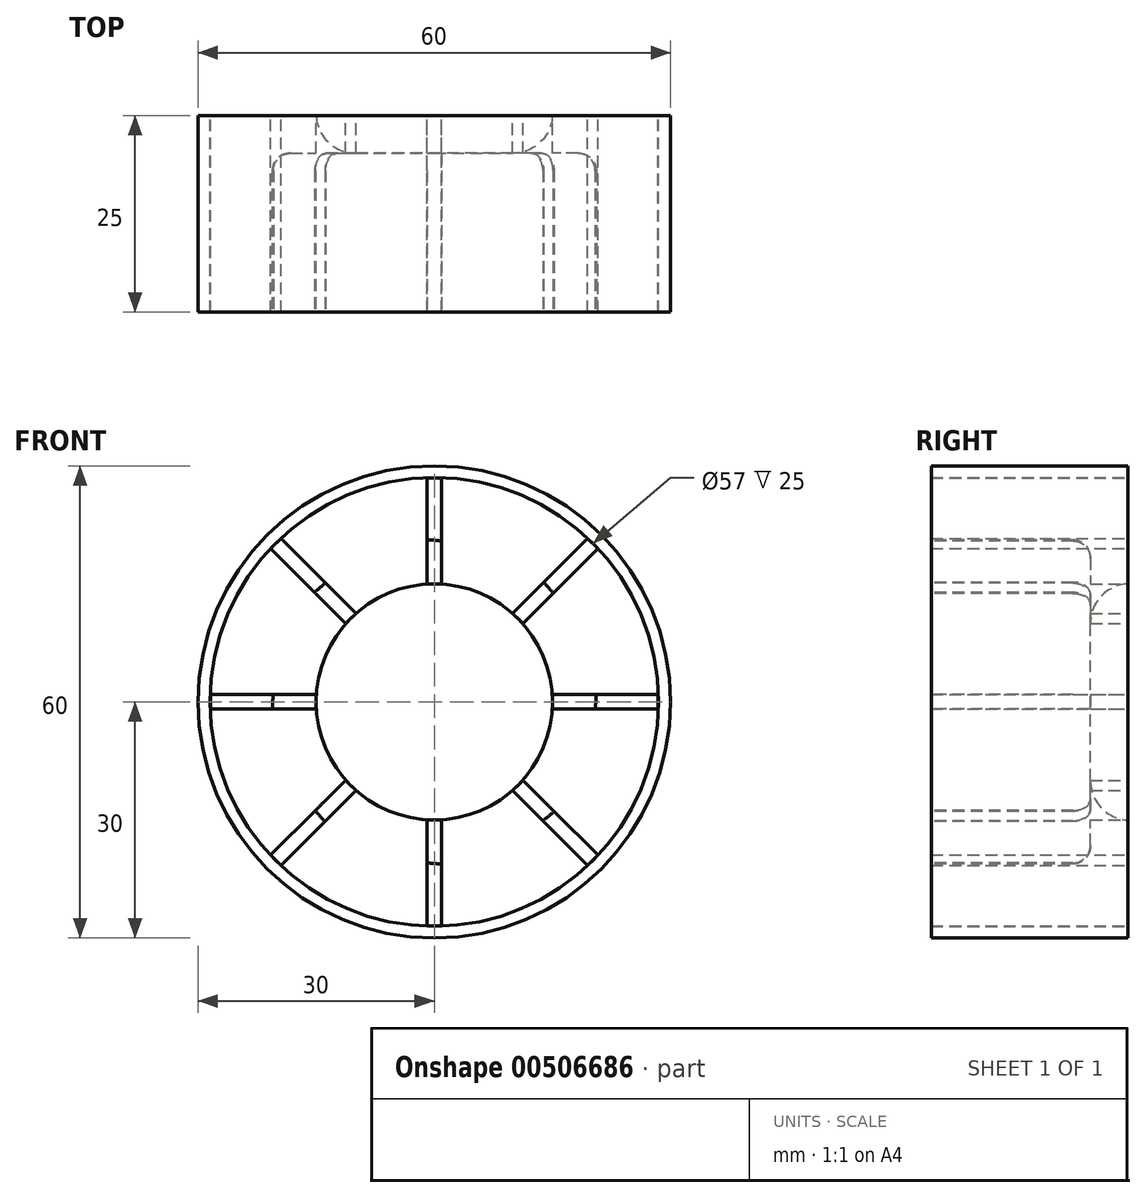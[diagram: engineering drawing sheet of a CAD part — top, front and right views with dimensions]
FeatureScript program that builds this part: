
annotation { "Feature Type Name" : "Feature", "Feature Type Description" : "" }
export const myFeature = defineFeature(function(context is Context, id is Id, definition is map)
    precondition{}
    {
        {
            var Q0;
            Q0=qCreatedBy(makeId("Front.planeOp"),FACE);
            var sketch = newSketch(context, id + "F0", { "sketchPlane" : qUnion([Q0])});
            skCircle(sketch, "E0", {"center": v(0, 0) * mm, "radius": 30 * mm});
            skSolve(sketch);
        }
        {
            var Q0;
            Q0=makeQuery(id+"F0.imprint","IMPRINT",FACE,{"disambiguationData":[TD([[makeQuery(id+"F0.imprint","IMPRINT",EDGE,{"derivedFrom":sQuery(id+"F0.wireOp",EDGE,"E0")}),1.0]])]});
            extrude(context, id + "F1", {"entities" : qUnion([Q0]), "depth" : 25 * mm});
        }
        {
            var Q0;
            Q0=qCreatedBy(makeId("Front.planeOp"),FACE);
            var sketch = newSketch(context, id + "F2", { "sketchPlane" : qUnion([Q0])});
            skCircle(sketch, "E1", {"center": v(0, 0) * mm, "radius": 28.5 * mm});
            skSolve(sketch);
        }
        {
            var Q0;
            Q0 = qSketchRegion(id + "F2", true);
            extrude(context, id + "F3", {"entities" : qUnion([Q0]), "operationType" : NewBodyOperationType.REMOVE, "depth" : 43.4 * mm});
        }
        {
            var Q0;
            Q0=qCreatedBy(makeId("Front.planeOp"),FACE);
            var sketch = newSketch(context, id + "F4", { "sketchPlane" : qUnion([Q0])});
            skCircle(sketch, "E2", {"center": v(0, 0) * mm, "radius": 15 * mm});
            skSolve(sketch);
        }
        {
            var Q0;
            Q0=makeQuery(id+"F4.imprint","IMPRINT",FACE,{"disambiguationData":[TD([[makeQuery(id+"F4.imprint","IMPRINT",EDGE,{"derivedFrom":sQuery(id+"F4.wireOp",EDGE,"E2")}),1.0]])]});
            extrude(context, id + "F5", {"entities" : qUnion([Q0]), "depth" : 5 * mm});
        }
        {
            var Q0;
            Q0=qCreatedBy(makeId("Front.planeOp"),FACE);
            var sketch = newSketch(context, id + "F6", { "sketchPlane" : qUnion([Q0])});
            skLineSegment(sketch, "E3.bottom", {"start": v(0.92, 28.44) * mm, "end": v(-0.92, 28.44) * mm});
            skLineSegment(sketch, "E3.top", {"start": v(0.92, 15.01) * mm, "end": v(-0.92, 15.01) * mm});
            skLineSegment(sketch, "E3.left", {"start": v(0.92, 28.44) * mm, "end": v(0.92, 15.01) * mm});
            skLineSegment(sketch, "E3.right", {"start": v(-0.92, 28.44) * mm, "end": v(-0.92, 15.01) * mm});
            skSolve(sketch);
        }
        {
            var Q0;
            Q0=makeQuery(id+"F6.imprint","IMPRINT",FACE,{"disambiguationData":[TD([[makeQuery(id+"F6.imprint","IMPRINT",EDGE,{"derivedFrom":sQuery(id+"F6.wireOp",EDGE,"E3.bottom")}),1.0]])]});
            extrude(context, id + "F7", {"entities" : qUnion([Q0]), "depth" : 25 * mm});
        }
        {
            var Q0;
            Q0=makeQuery(id+"F1.opExtrude","CAP_FACE",FACE,{"disambiguationData":[OSD([sQuery(id+"F0.wireOp",EDGE,"E0")])],"isStart":false});
            var sketch = newSketch(context, id + "F8", { "sketchPlane" : qUnion([Q0])});
            skCircle(sketch, "E4", {"center": v(-1.8, -3.51) * mm, "radius": 24.1 * mm});
            skSolve(sketch);
        }
        {
            var Q0;
            Q0 = qSketchRegion(id + "F8", true);
            extrude(context, id + "F9", {"entities" : qUnion([Q0]), "operationType" : NewBodyOperationType.REMOVE, "oppositeDirection" : true, "depth" : 20.2 * mm});
        }
        {
            var Q0;
            Q0=makeQuery(id+"F9.boolean.opBoolean","COPY",EDGE,{"derivedFrom":makeQuery(id+"F9.opExtrude","CAP_EDGE",EDGE,{"disambiguationData":[OSD([sQuery(id+"F8.wireOp",EDGE,"E4")])],"isStart":false})});
            var Q1;
            Q1=makeQuery(id+"F9.boolean.opBoolean","COPY",FACE,{"derivedFrom":makeQuery(id+"F9.opExtrude","SWEPT_FACE",FACE,{"disambiguationData":[OSD([sQuery(id+"F8.wireOp",EDGE,"E4")])]})});
            var Q2;
            Q2=makeQuery(id+"F9.boolean.opBoolean","COPY",FACE,{"derivedFrom":makeQuery(id+"F9.opExtrude","CAP_FACE",FACE,{"disambiguationData":[OSD([sQuery(id+"F8.wireOp",EDGE,"E4")])],"isStart":false})});
            fillet(context, id + "F10", {"entities" : qUnion([Q0, Q1, Q2]), "radius" : 5 * mm, "tangentPropagation" : true, "allowEdgeOverflow" : false});
        }
        {
            var Q0;
            Q0=makeQuery(id+"F9.boolean.opBoolean","COPY",EDGE,{"derivedFrom":makeQuery(id+"F9.opExtrude","CAP_EDGE",EDGE,{"disambiguationData":[OSD([sQuery(id+"F8.wireOp",EDGE,"E4")])],"isStart":false})});
            fillet(context, id + "F11", {"entities" : qUnion([Q0]), "radius" : 2.2 * mm, "tangentPropagation" : true, "allowEdgeOverflow" : false});
        }
        {
            var Q0;
            Q0=makeQuery(id+"F7.opExtrude","SWEPT_BODY",BODY,{"disambiguationData":[OSD([sQuery(id+"F6.wireOp",EDGE,"E3.bottom"),sQuery(id+"F6.wireOp",EDGE,"E3.top"),sQuery(id+"F6.wireOp",EDGE,"E3.left"),sQuery(id+"F6.wireOp",EDGE,"E3.right")])]});
            var Q1;
            Q1=makeQuery(id+"F3.boolean.opBoolean","COPY",FACE,{"derivedFrom":makeQuery(id+"F3.opExtrude","SWEPT_FACE",FACE,{"disambiguationData":[OSD([sQuery(id+"F2.wireOp",EDGE,"E1")])]})});
            circularPattern(context, id + "F12", {"entities" : qUnion([Q0]), "axis" : qUnion([Q1]), "angle" : 360 * degree, "instanceCount" : 8, "equalSpace" : true});
        }
    });
